# Revit family: Kabelrinnen-Systeme_Magic_Bogen 45° Magic_610
name_source: partatom
category: Generic Models
revit_build: Autodesk Revit 2015 (Build: 20140606_1530(x64)
units: mm (PartAtom-declared; Revit-internal decimal feet)

## types (14) — shared parameters
Manufacturer = OBO Bettermann
Material = Steel, Galvanized
URL = http://www.obo-bettermann.com

## per-type parameters (varying)
| type | B | GTIN | Manufacturer Art. No. |
| RBM 45 610 FS | 100 mm  [stored 0.328084 ft] | 4012195881537 | 6041040 |
| RBM 45 615 FS | 150 mm | 4012195881544 | 6041042 |
| RBM 45 620 FS | 200 mm  [stored 0.656168 ft] | 4012195881551 | 6041044 |
| RBM 45 630 FS | 300 mm | 4012195881568 | 6041046 |
| RBM 45 640 FS | 400 mm  [stored 1.31234 ft] | 4012195881575 | 6041048 |
| RBM 45 650 FS | 500 mm  [stored 1.64042 ft] | 4012195881582 | 6041050 |
| RBM 45 660 FS | 600 mm | 4012195881599 | 6041052 |
| RBM 45 610 FT | 100 mm  [stored 0.328084 ft] | 4012195881605 | 6041060 |
| RBM 45 615 FT | 150 mm | 4012195881612 | 6041062 |
| RBM 45 620 FT | 200 mm  [stored 0.656168 ft] | 4012195881629 | 6041064 |
| RBM 45 630 FT | 300 mm | 4012195881636 | 6041066 |
| RBM 45 640 FT | 400 mm  [stored 1.31234 ft] | 4012195881643 | 6041068 |
| RBM 45 650 FT | 500 mm  [stored 1.64042 ft] | 4012195881650 | 6041070 |
| RBM 45 660 FT | 600 mm | 4012195881667 | 6041072 |

note: column(s) folded — value = type name in every type: Article Type

note: [stored X ft] marks values corroborated as IEEE doubles in the binary element streams (Revit-internal decimal feet)

## geometry (parser evidence)
native form markers: Sweep x1
no freeform markers — native parametric forms only
